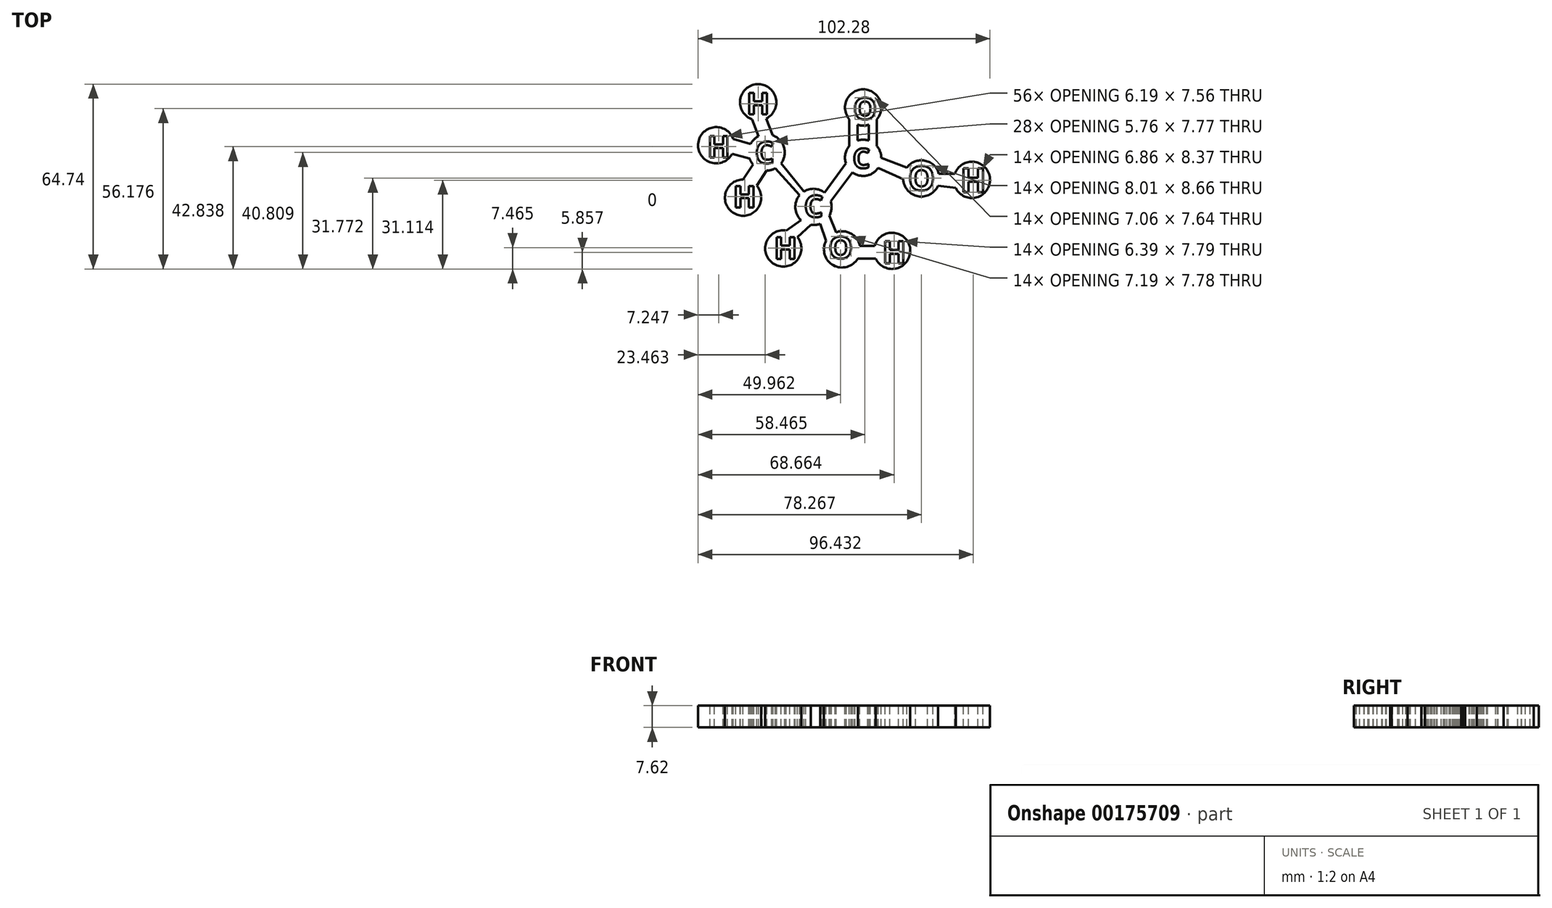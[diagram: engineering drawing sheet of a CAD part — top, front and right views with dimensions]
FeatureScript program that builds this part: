
annotation { "Feature Type Name" : "Feature", "Feature Type Description" : "" }
export const myFeature = defineFeature(function(context is Context, id is Id, definition is map)
    precondition{}
    {
        {
            var Q0;
            Q0=qCreatedBy(makeId("Top.planeOp"),FACE);
            var sketch = newSketch(context, id + "F0", { "sketchPlane" : qUnion([Q0])});
            skCircle(sketch, "E0", {"center": v(-46.64, 11.66) * mm, "radius": 6.35 * mm});
            skCircle(sketch, "E1", {"center": v(-30.25, -7.42) * mm, "radius": 6.35 * mm});
            skCircle(sketch, "E2", {"center": v(-12.84, 9.8) * mm, "radius": 6.35 * mm});
            skCircle(sketch, "E3", {"center": v(-12.84, 27.42) * mm, "radius": 6.35 * mm});
            skCircle(sketch, "E4", {"center": v(7.57, 2.56) * mm, "radius": 6.35 * mm});
            skCircle(sketch, "E5", {"center": v(25.26, 2.05) * mm, "radius": 6.35 * mm});
            skCircle(sketch, "E6", {"center": v(-20.21, -22.3) * mm, "radius": 6.35 * mm});
            skCircle(sketch, "E7", {"center": v(-2.7, -22.8) * mm, "radius": 6.35 * mm});
            skCircle(sketch, "E8", {"center": v(-40.81, -21.98) * mm, "radius": 6.35 * mm});
            skCircle(sketch, "E9", {"center": v(-49.62, 29.23) * mm, "radius": 6.35 * mm});
            skCircle(sketch, "E10", {"center": v(-64.32, 14.18) * mm, "radius": 6.35 * mm});
            skCircle(sketch, "E11", {"center": v(-54.9, -4.17) * mm, "radius": 6.35 * mm});
            skLineSegment(sketch, "E12", {"start": v(-51.78, 23.26) * mm, "end": v(-49.48, 17.34) * mm});
            skLineSegment(sketch, "E13", {"start": v(-46.82, 23.53) * mm, "end": v(-44.48, 17.63) * mm});
            skLineSegment(sketch, "E14", {"start": v(-58.36, 16.36) * mm, "end": v(-52.24, 14.65) * mm});
            skLineSegment(sketch, "E15", {"start": v(-58.72, 11.19) * mm, "end": v(-52.6, 9.47) * mm});
            skLineSegment(sketch, "E16", {"start": v(-54.94, 2.18) * mm, "end": v(-51.38, 7.44) * mm});
            skLineSegment(sketch, "E17", {"start": v(-50.11, 0) * mm, "end": v(-46.63, 5.3) * mm});
            skLineSegment(sketch, "E18", {"start": v(-43.67, 6.05) * mm, "end": v(-35.13, -3.35) * mm});
            skLineSegment(sketch, "E19", {"start": v(-41.55, 7.87) * mm, "end": v(-33.54, -1.99) * mm});
            skLineSegment(sketch, "E20", {"start": v(-39.8, -15.71) * mm, "end": v(-34.63, -12.02) * mm});
            skLineSegment(sketch, "E21", {"start": v(-35.9, -17.97) * mm, "end": v(-31.19, -13.7) * mm});
            skLineSegment(sketch, "E22", {"start": v(-26.32, -2.44) * mm, "end": v(-18.9, 7.87) * mm});
            skLineSegment(sketch, "E23", {"start": v(-24.2, -5.5) * mm, "end": v(-16.63, 4.7) * mm});
            skLineSegment(sketch, "E24", {"start": v(-27.93, -13.33) * mm, "end": v(-25.82, -19.32) * mm});
            skLineSegment(sketch, "E25", {"start": v(-24.64, -10.4) * mm, "end": v(-22.35, -16.32) * mm});
            skLineSegment(sketch, "E26", {"start": v(-14, -21.02) * mm, "end": v(-8.79, -21.02) * mm});
            skLineSegment(sketch, "E27", {"start": v(-14.72, -25.48) * mm, "end": v(-8.45, -25.48) * mm});
            skLineSegment(sketch, "E28", {"start": v(-17.68, 23.3) * mm, "end": v(-17.68, 13.9) * mm});
            skLineSegment(sketch, "E29", {"start": v(-10.87, 21.38) * mm, "end": v(-10.87, 15.83) * mm});
            skLineSegment(sketch, "E30", {"start": v(-8, 23.3) * mm, "end": v(-8, 13.9) * mm});
            skLineSegment(sketch, "E31", {"start": v(-6.5, 9.8) * mm, "end": v(2.43, 6.3) * mm});
            skLineSegment(sketch, "E32", {"start": v(-7.61, 6.2) * mm, "end": v(1.22, 2.28) * mm});
            skLineSegment(sketch, "E33", {"start": v(13.71, 4.16) * mm, "end": v(19.27, 4.16) * mm});
            skLineSegment(sketch, "E34", {"start": v(13.37, 0) * mm, "end": v(19.59, -0.8) * mm});
            skText(sketch, "E35", { "text": "H", "fontName": "OpenSans-Bold.ttf"});
            skText(sketch, "E36", { "text": "H", "fontName": "OpenSans-Bold.ttf"});
            skText(sketch, "E37", { "text": "H", "fontName": "OpenSans-Bold.ttf"});
            skText(sketch, "E38", { "text": "C", "fontName": "OpenSans-Bold.ttf"});
            skText(sketch, "E39", { "text": "H", "fontName": "OpenSans-Bold.ttf"});
            skText(sketch, "E40", { "text": "C", "fontName": "OpenSans-Bold.ttf"});
            skText(sketch, "E41", { "text": "C", "fontName": "OpenSans-Bold.ttf"});
            skText(sketch, "E42", { "text": "O", "fontName": "OpenSans-Bold.ttf"});
            skText(sketch, "E43", { "text": "O", "fontName": "OpenSans-Bold.ttf"});
            skText(sketch, "E44", { "text": "H", "fontName": "OpenSans-Bold.ttf"});
            skText(sketch, "E45", { "text": "O", "fontName": "OpenSans-Bold.ttf"});
            skText(sketch, "E46", { "text": "H", "fontName": "OpenSans-Bold.ttf"});
            skLineSegment(sketch, "E47", {"start": v(-14.82, 21.38) * mm, "end": v(-14.82, 15.83) * mm});
            const initialGuessF0  = {"E35": [-0.0537, 0.02498, 1, 0, 0.00762], "E36": [-0.06747, 0.0099, 1, 0, 0.00762], "E37": [-0.0584, -0.00762, 1, 0, 0.00762], "E38": [-0.0507, 0.00787, 1, 0, 0.00762], "E39": [-0.0441, -0.02559, 1, 0, 0.00762], "E40": [-0.03354, -0.01097, 1, 0, 0.00762], "E41": [-0.01652, 0.00616, 1, 0, 0.00693], "E42": [-0.02492, -0.02548, 1, 0, 0.00762], "E43": [-0.01634, 0.0233, 1, 0, 0.00748], "E44": [-0.00618, -0.0272, 1, 0, 0.00786], "E45": [0.00291, -0.0016, 1, 0, 0.00848], "E46": [0.02128, -0.00223, 1, 0, 0.00844]};
            skSetInitialGuess(sketch, initialGuessF0);
            skSolve(sketch);
        }
        {
            var Q0;
            Q0 = qSketchRegion(id + "F0", true);
            extrude(context, id + "F1", {"entities" : qUnion([Q0]), "oppositeDirection" : true, "depth" : 7.62 * mm});
        }
        {
            var Q0;
            Q0=makeQuery(id+"F0.imprint","IMPRINT",FACE,{"disambiguationData":[TD([[makeQuery(id+"F0.imprint","IMPRINT",EDGE,{"derivedFrom":sQuery(id+"F0.wireOp",EDGE,"E43.sketch_text.stroke-8")}),1.0]])]});
            extrude(context, id + "F2", {"entities" : qUnion([Q0]), "oppositeDirection" : true, "depth" : 7.62 * mm});
        }
        {
            var Q0;
            Q0=makeQuery(id+"F0.imprint","IMPRINT",FACE,{"disambiguationData":[TD([[makeQuery(id+"F0.imprint","IMPRINT",EDGE,{"derivedFrom":sQuery(id+"F0.wireOp",EDGE,"E45.sketch_text.stroke-8")}),1.0]])]});
            extrude(context, id + "F3", {"entities" : qUnion([Q0]), "oppositeDirection" : true, "depth" : 7.62 * mm});
        }
        {
            var Q0;
            Q0=makeQuery(id+"F0.imprint","IMPRINT",FACE,{"disambiguationData":[TD([[makeQuery(id+"F0.imprint","IMPRINT",EDGE,{"derivedFrom":sQuery(id+"F0.wireOp",EDGE,"E42.sketch_text.stroke-8")}),1.0]])]});
            extrude(context, id + "F4", {"entities" : qUnion([Q0]), "oppositeDirection" : true, "depth" : 7.62 * mm});
        }
    });
